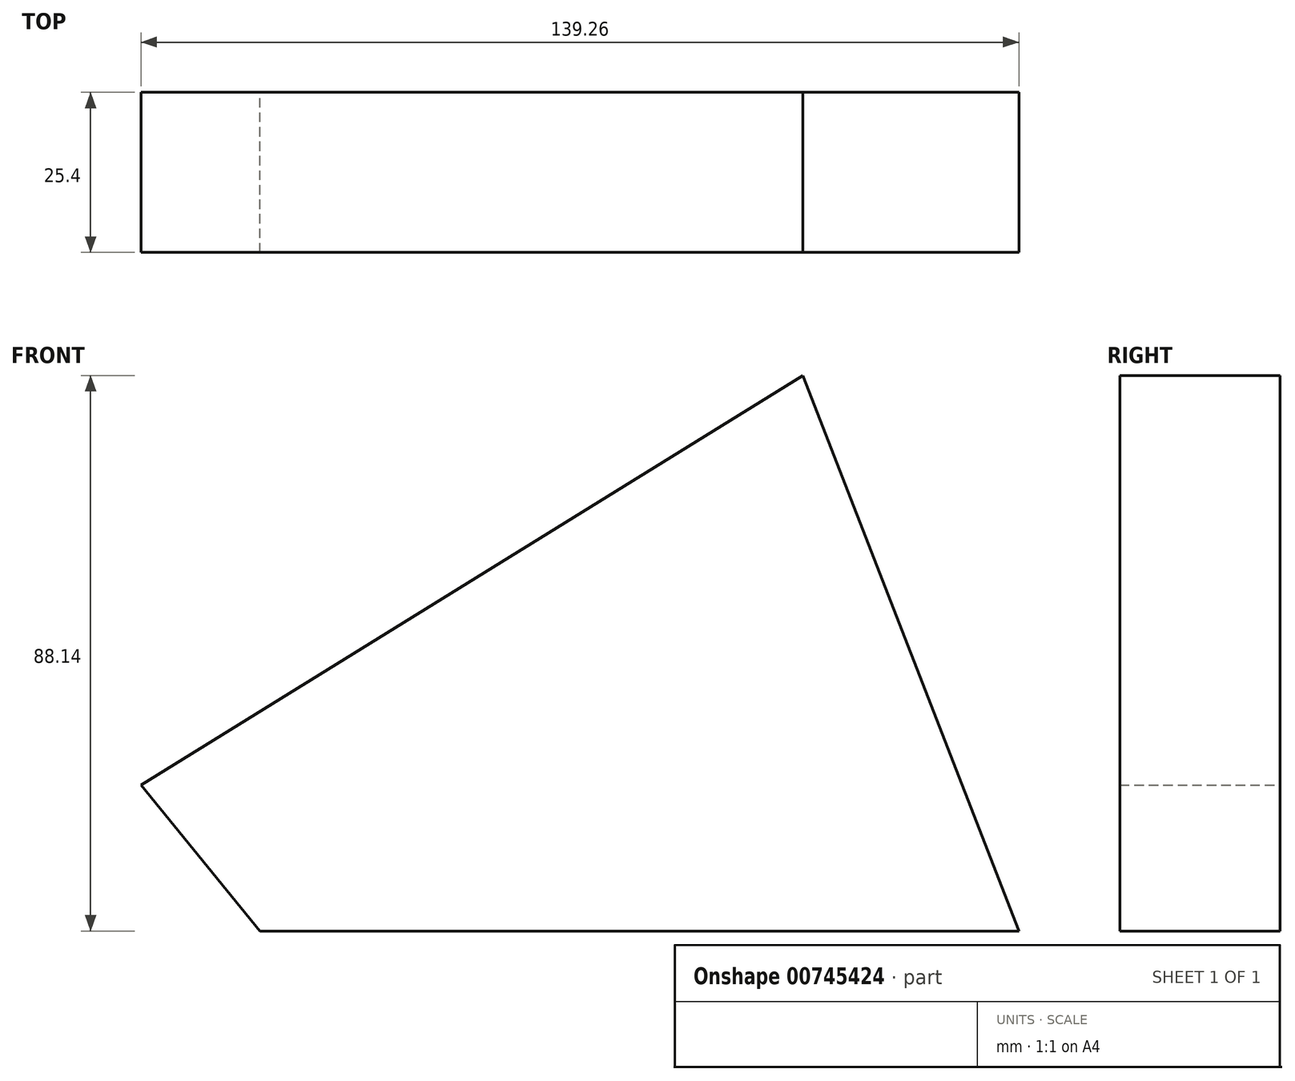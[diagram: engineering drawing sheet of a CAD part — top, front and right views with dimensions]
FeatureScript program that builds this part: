
annotation { "Feature Type Name" : "Feature", "Feature Type Description" : "" }
export const myFeature = defineFeature(function(context is Context, id is Id, definition is map)
    precondition{}
    {
        {
            var Q0;
            Q0=qCreatedBy(makeId("Front.planeOp"),FACE);
            var sketch = newSketch(context, id + "F0", { "sketchPlane" : qUnion([Q0])});
            skLineSegment(sketch, "E0", {"start": v(47.88, -20.2) * mm, "end": v(13.59, 67.94) * mm});
            skLineSegment(sketch, "E1", {"start": v(47.88, -20.2) * mm, "end": v(-72.52, -20.2) * mm});
            skLineSegment(sketch, "E2", {"start": v(-72.52, -20.2) * mm, "end": v(-91.38, 2.95) * mm});
            skLineSegment(sketch, "E3", {"start": v(-91.38, 2.95) * mm, "end": v(179.36, -23.73) * mm});
            skLineSegment(sketch, "E4", {"start": v(179.36, -23.73) * mm, "end": v(177.37, -43.92) * mm});
            skLineSegment(sketch, "E5", {"start": v(177.37, -43.92) * mm, "end": v(-91.38, -20.2) * mm});
            skLineSegment(sketch, "E6", {"start": v(-91.38, -20.2) * mm, "end": v(-91.38, 2.95) * mm});
            skLineSegment(sketch, "E7", {"start": v(-91.38, 2.95) * mm, "end": v(13.59, 67.94) * mm});
            skSolve(sketch);
        }
        {
            var Q0;
            {var subQ0=sQuery(id+"F0.wireOp",EDGE,"E1");Q0=makeQuery(id+"F0.imprint","IMPRINT",FACE,{"disambiguationData":[TD([[makeQuery(id+"F0.imprint","IMPRINT",EDGE,{"derivedFrom":subQ0}),-1.0]])]});}
            var Q1;
            {var subQ0=sQuery(id+"F0.wireOp",EDGE,"E7");Q1=makeQuery(id+"F0.imprint","IMPRINT",FACE,{"disambiguationData":[TD([[makeQuery(id+"F0.imprint","IMPRINT",EDGE,{"derivedFrom":subQ0}),-1.0]])]});}
            extrude(context, id + "F1", {"entities" : qUnion([Q0, Q1]), "depth" : 25.4 * mm, "offsetDistance" : 25.4 * mm});
        }
    });
